# Revit family: 1326054 - Kos Square 140 LED
name_source: partatom
category: Lighting Fixtures
units: mm (PartAtom-declared; Revit-internal decimal feet)

## family parameters
Always vertical = Yes
Cut with Voids When Loaded = No
Host = Ceiling
Light Source = Yes
OmniClass Number = 23.80.70.11
OmniClass Title = Luminaries for Internal Lighting
Part Type = Normal
Room Calculation Point = No
Round Connector Dimension = Use Diameter
Shared = No

## types (2) — shared parameters
Apparent Load = 12 VA
Color Filter = 16777215
Dimmable = Yes
Dimming Lamp Color Temperature Shift = <None>
Driver Included = Yes (Integral)
Driver Required = No
Lamp = LED
Light Source Fixed = Yes
Main Finish = Textured White
Product Name = Kos Square 140 LED
Tilt Angle = 90.00°
zero-valued in all types: Default Elevation

## per-type parameters (varying)
| type | ADA compliant | Dimming Method | Efficacy (lm/w) | Electrical Class | Location Rating | Main Material | Photometric Web File | Power (Watts) | Product Code | Product Location | Product SKU | Wattage Comments |
| CE |  | Phase - Leading & Trailing Edge
Phase - Leading & Trailing Edge | 62.17 | CE (Class II) | IP65 | Metal - Aluminium
Metal - Aluminium
Metal - Aluminium
Metal - Aluminium
Metal - Aluminium | IES-GNC-21860 Kos Round 140 inc Sphere spectra.ies | 12.4 | 8516 | Architectural / Bathroom / Indoor / Outdoor | 1326022 |  |
| ETL | No | Phase - Leading & Trailing Edge | 80 | cULus (Class 1) | WET | Metal - Aluminium | TE079-068-PW08_EDC47C-12W-930-120V-B_200803_IESNA95.IES | 11.8 | 1326054 | Architectural, Bathroom, Indoor, Outdoor | 1326054 | Measured |

## geometry (parser evidence)
native form markers: Sweep x2
no freeform markers — native parametric forms only
